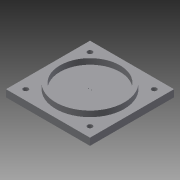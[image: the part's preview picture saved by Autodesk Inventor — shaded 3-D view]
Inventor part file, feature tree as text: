
AUTODESK INVENTOR PART (.ipt)
format: ipt  version: 2015 (Build 190159000, 159)  size: 105,984 bytes
history: native  units: in
note: dims shown in document units (in); Inventor stores cm internally (conversion verified against a paired STEP export)
features: extrude x2, sketch x2
ambient origin geometry x8: Origin, YZ Plane, XZ Plane, XY Plane, X Axis, Y Axis, Z Axis, Center Point
bodies: Solid1 (feature_tree)
feature tree (4):
  extrude  "Extrusion1"  Depth=0.1969in TaperAngle=0.0deg
  extrude  "Extrusion2"  Depth=0.0394in
  sketch  "Sketch1"  dims[d0=2.3425in d1=0.1969in d2=0.0in]
  sketch  "Sketch3"  dims[d3=0.1378in d4=0.2756in d5=0.2756in d7=0.1181in d8=0.1575in d9=0.0in d10=0.0394in d11=0.0197in d12=0.2165in]
